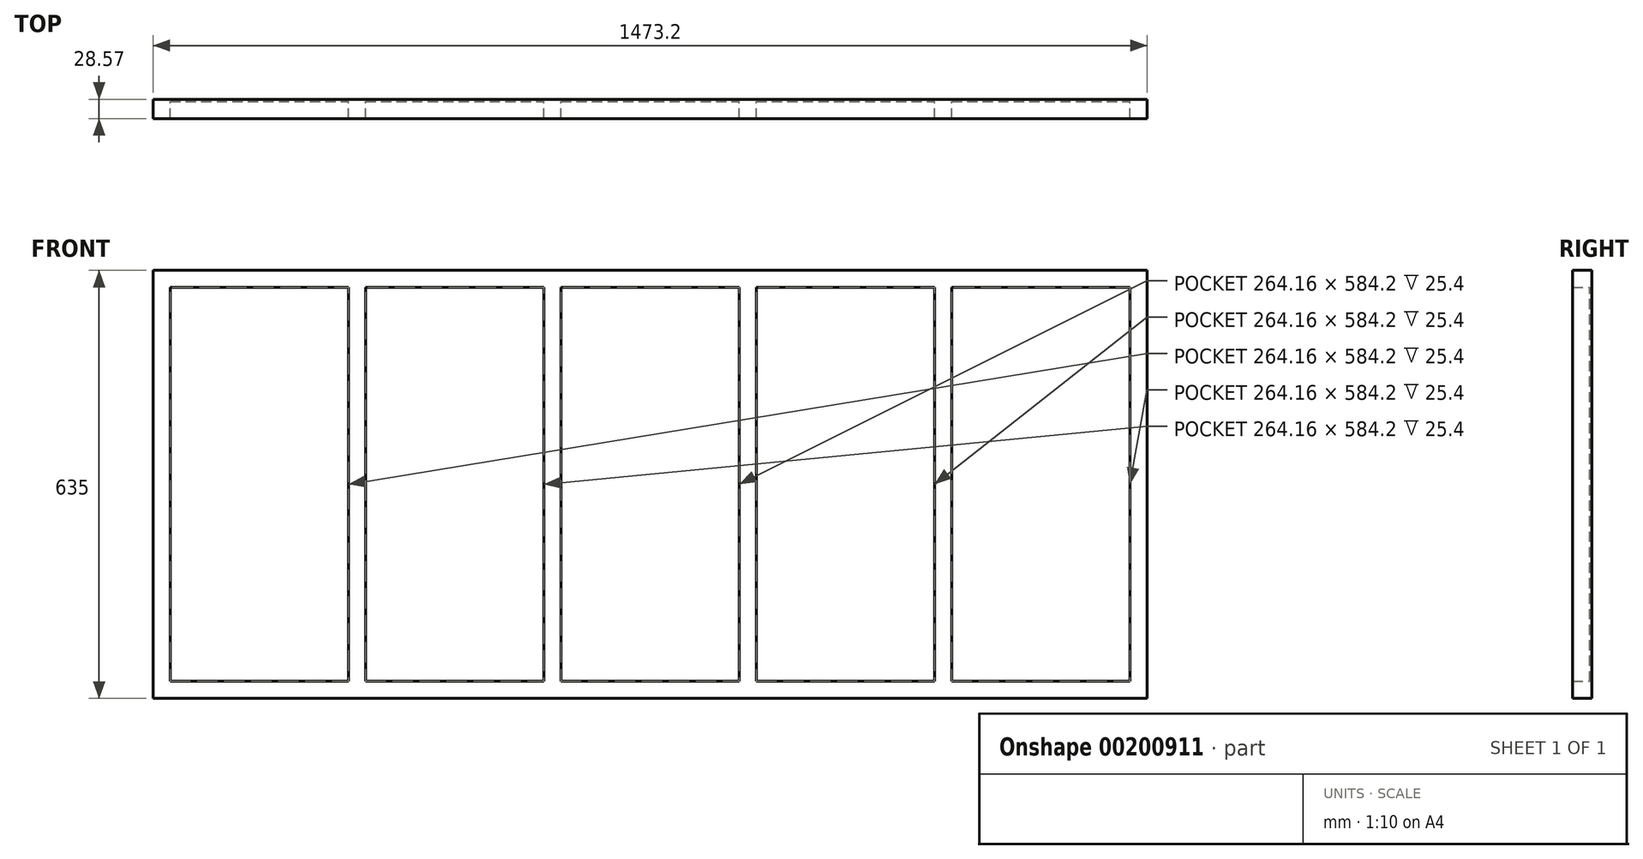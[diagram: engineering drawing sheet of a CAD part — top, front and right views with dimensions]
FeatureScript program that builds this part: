
annotation { "Feature Type Name" : "Feature", "Feature Type Description" : "" }
export const myFeature = defineFeature(function(context is Context, id is Id, definition is map)
    precondition{}
    {
        {
            var Q0;
            Q0=qCreatedBy(makeId("Front.planeOp"),FACE);
            var sketch = newSketch(context, id + "F0", { "sketchPlane" : qUnion([Q0])});
            skLineSegment(sketch, "E0.bottom", {"start": v(0, 0) * mm, "end": v(1473.2, 0) * mm});
            skLineSegment(sketch, "E0.top", {"start": v(0, 635) * mm, "end": v(1473.2, 635) * mm});
            skLineSegment(sketch, "E0.left", {"start": v(0, 0) * mm, "end": v(0, 635) * mm});
            skLineSegment(sketch, "E0.right", {"start": v(1473.2, 0) * mm, "end": v(1473.2, 635) * mm});
            skSolve(sketch);
        }
        {
            var Q0;
            Q0=makeQuery(id+"F0.imprint","IMPRINT",FACE,{"disambiguationData":[TD([[makeQuery(id+"F0.imprint","IMPRINT",EDGE,{"derivedFrom":sQuery(id+"F0.wireOp",EDGE,"E0.bottom")}),1.0]])]});
            extrude(context, id + "F1", {"entities" : qUnion([Q0]), "depth" : 3.17 * mm});
        }
        {
            var Q0;
            Q0=makeQuery(id+"F1.opExtrude","CAP_FACE",FACE,{"disambiguationData":[OSD([sQuery(id+"F0.wireOp",EDGE,"E0.bottom"),sQuery(id+"F0.wireOp",EDGE,"E0.top"),sQuery(id+"F0.wireOp",EDGE,"E0.left"),sQuery(id+"F0.wireOp",EDGE,"E0.right")])],"isStart":false});
            var sketch = newSketch(context, id + "F2", { "sketchPlane" : qUnion([Q0])});
            skLineSegment(sketch, "E1.bottom", {"start": v(0, 0) * mm, "end": v(1473.2, 0) * mm});
            skLineSegment(sketch, "E1.top", {"start": v(0, 25.4) * mm, "end": v(1473.2, 25.4) * mm});
            skLineSegment(sketch, "E1.left", {"start": v(0, 0) * mm, "end": v(0, 25.4) * mm});
            skLineSegment(sketch, "E1.right", {"start": v(1473.2, 0) * mm, "end": v(1473.2, 25.4) * mm});
            skLineSegment(sketch, "E2.bottom", {"start": v(0, 635) * mm, "end": v(1473.2, 635) * mm});
            skLineSegment(sketch, "E2.top", {"start": v(0, 609.6) * mm, "end": v(1473.2, 609.6) * mm});
            skLineSegment(sketch, "E2.left", {"start": v(0, 635) * mm, "end": v(0, 609.6) * mm});
            skLineSegment(sketch, "E2.right", {"start": v(1473.2, 635) * mm, "end": v(1473.2, 609.6) * mm});
            skLineSegment(sketch, "E3.bottom", {"start": v(0, 25.4) * mm, "end": v(25.4, 25.4) * mm});
            skLineSegment(sketch, "E3.top", {"start": v(0, 609.6) * mm, "end": v(25.4, 609.6) * mm});
            skLineSegment(sketch, "E3.left", {"start": v(0, 25.4) * mm, "end": v(0, 609.6) * mm});
            skLineSegment(sketch, "E3.right", {"start": v(25.4, 25.4) * mm, "end": v(25.4, 609.6) * mm});
            skLineSegment(sketch, "E4.1.0.0", {"start": v(314.96, 25.4) * mm, "end": v(314.96, 609.6) * mm});
            skLineSegment(sketch, "E4.1.0.1", {"start": v(289.56, 25.4) * mm, "end": v(289.56, 609.6) * mm});
            skLineSegment(sketch, "E4.2.0.0", {"start": v(604.52, 25.4) * mm, "end": v(604.52, 609.6) * mm});
            skLineSegment(sketch, "E4.2.0.1", {"start": v(579.12, 25.4) * mm, "end": v(579.12, 609.6) * mm});
            skLineSegment(sketch, "E4.3.0.0", {"start": v(894.08, 25.4) * mm, "end": v(894.08, 609.6) * mm});
            skLineSegment(sketch, "E4.3.0.1", {"start": v(868.68, 25.4) * mm, "end": v(868.68, 609.6) * mm});
            skLineSegment(sketch, "E4.4.0.0", {"start": v(1183.64, 25.4) * mm, "end": v(1183.64, 609.6) * mm});
            skLineSegment(sketch, "E4.4.0.1", {"start": v(1158.24, 25.4) * mm, "end": v(1158.24, 609.6) * mm});
            skLineSegment(sketch, "E4.5.0.0", {"start": v(1473.2, 25.4) * mm, "end": v(1473.2, 609.6) * mm});
            skLineSegment(sketch, "E4.5.0.1", {"start": v(1447.8, 25.4) * mm, "end": v(1447.8, 609.6) * mm});
            skLineSegment(sketch, "E4.direction1", {"start": v(25.4, 25.4) * mm, "end": v(314.96, 25.4) * mm, "construction": true});
            skSolve(sketch);
        }
        {
            var Q0;
            Q0 = qSketchRegion(id + "F2", true);
            var Q1;
            {var subQ0=sQuery(id+"F2.wireOp",EDGE,"E4.1.0.0");Q1=makeQuery(id+"F2.imprint","IMPRINT",FACE,{"disambiguationData":[TD([[makeQuery(id+"F2.imprint","IMPRINT",EDGE,{"derivedFrom":subQ0}),1.0]])]});}
            var Q2;
            {var subQ0=sQuery(id+"F2.wireOp",EDGE,"E4.2.0.0");Q2=makeQuery(id+"F2.imprint","IMPRINT",FACE,{"disambiguationData":[TD([[makeQuery(id+"F2.imprint","IMPRINT",EDGE,{"derivedFrom":subQ0}),1.0]])]});}
            var Q3;
            {var subQ0=sQuery(id+"F2.wireOp",EDGE,"E4.3.0.0");Q3=makeQuery(id+"F2.imprint","IMPRINT",FACE,{"disambiguationData":[TD([[makeQuery(id+"F2.imprint","IMPRINT",EDGE,{"derivedFrom":subQ0}),1.0]])]});}
            var Q4;
            {var subQ0=sQuery(id+"F2.wireOp",EDGE,"E4.4.0.0");Q4=makeQuery(id+"F2.imprint","IMPRINT",FACE,{"disambiguationData":[TD([[makeQuery(id+"F2.imprint","IMPRINT",EDGE,{"derivedFrom":subQ0}),1.0]])]});}
            extrude(context, id + "F3", {"entities" : qUnion([Q0, Q1, Q2, Q3, Q4]), "operationType" : NewBodyOperationType.ADD, "depth" : 25.4 * mm});
        }
    });
